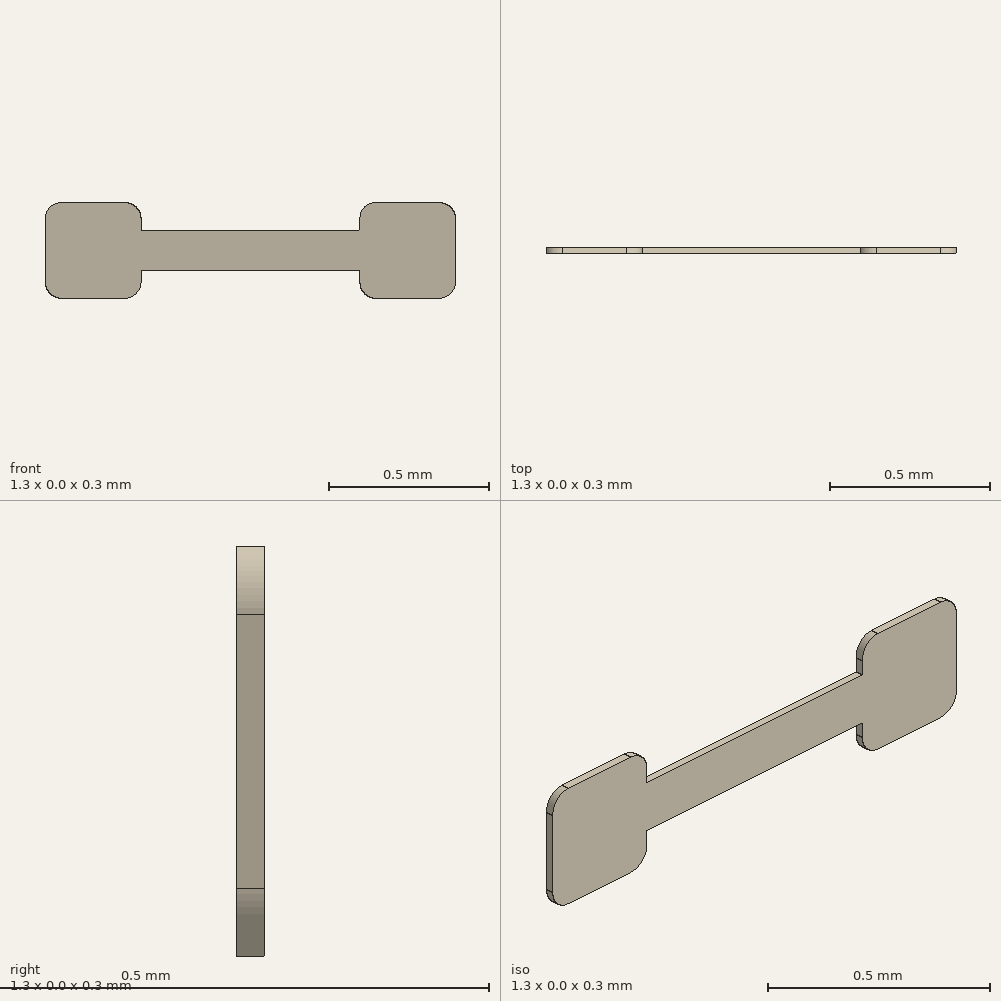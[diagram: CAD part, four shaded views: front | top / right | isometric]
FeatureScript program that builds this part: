
annotation { "Feature Type Name" : "Feature", "Feature Type Description" : "" }
export const myFeature = defineFeature(function(context is Context, id is Id, definition is map)
    precondition{}
    {
        {
            var Q0;
            Q0=qCreatedBy(makeId("Front.planeOp"),FACE);
            var sketch = newSketch(context, id + "F0", { "sketchPlane" : qUnion([Q0])});
            skLineSegment(sketch, "E0.bottom", {"start": v(0.05, 0) * mm, "end": v(0.25, 0) * mm});
            skLineSegment(sketch, "E0.top", {"start": v(0.05, 0.3) * mm, "end": v(0.25, 0.3) * mm});
            skLineSegment(sketch, "E0.left", {"start": v(0, 0.05) * mm, "end": v(0, 0.25) * mm});
            skLineSegment(sketch, "E0.right", {"start": v(0.3, 0.05) * mm, "end": v(0.3, 0.25) * mm});
            skLineSegment(sketch, "E1.bottom", {"start": v(0.3, 0.21) * mm, "end": v(0.99, 0.21) * mm});
            skLineSegment(sketch, "E1.top", {"start": v(0.3, 0.09) * mm, "end": v(0.99, 0.09) * mm});
            skLineSegment(sketch, "E1.left", {"start": v(0.3, 0.21) * mm, "end": v(0.3, 0.09) * mm});
            skLineSegment(sketch, "E1.right", {"start": v(0.99, 0.21) * mm, "end": v(0.99, 0.09) * mm});
            skLineSegment(sketch, "E2.bottom", {"start": v(1.04, 0.3) * mm, "end": v(1.24, 0.3) * mm});
            skLineSegment(sketch, "E2.top", {"start": v(1.04, 0) * mm, "end": v(1.24, 0) * mm});
            skLineSegment(sketch, "E2.left", {"start": v(0.99, 0.25) * mm, "end": v(0.99, 0.05) * mm});
            skLineSegment(sketch, "E2.right", {"start": v(1.29, 0.25) * mm, "end": v(1.29, 0.05) * mm});
            skLineSegment(sketch, "E3", {"start": v(0.3, 0.15) * mm, "end": v(0.99, 0.15) * mm, "construction": true});
            skPoint(sketch, "E4.visualSharp", {"position": v(0, 0.3) * mm});
            skArc(sketch, "E4.filletArc", {"start": v(0.05, 0.3) * mm, "mid": v(0.01, 0.29) * mm, "end": v(0, 0.25) * mm});
            skPoint(sketch, "E5.visualSharp", {"position": v(0.3, 0.3) * mm});
            skArc(sketch, "E5.filletArc", {"start": v(0.3, 0.25) * mm, "mid": v(0.29, 0.29) * mm, "end": v(0.25, 0.3) * mm});
            skPoint(sketch, "E6.visualSharp", {"position": v(0, 0) * mm});
            skArc(sketch, "E6.filletArc", {"start": v(0, 0.05) * mm, "mid": v(0.01, 0.01) * mm, "end": v(0.05, 0) * mm});
            skPoint(sketch, "E7.visualSharp", {"position": v(0.3, 0) * mm});
            skArc(sketch, "E7.filletArc", {"start": v(0.25, 0) * mm, "mid": v(0.29, 0.01) * mm, "end": v(0.3, 0.05) * mm});
            skPoint(sketch, "E8.visualSharp", {"position": v(0.99, 0.3) * mm});
            skArc(sketch, "E8.filletArc", {"start": v(1.04, 0.3) * mm, "mid": v(1, 0.29) * mm, "end": v(0.99, 0.25) * mm});
            skPoint(sketch, "E9.visualSharp", {"position": v(0.99, 0) * mm});
            skArc(sketch, "E9.filletArc", {"start": v(0.99, 0.05) * mm, "mid": v(1, 0.01) * mm, "end": v(1.04, 0) * mm});
            skPoint(sketch, "E10.visualSharp", {"position": v(1.29, 0) * mm});
            skArc(sketch, "E10.filletArc", {"start": v(1.24, 0) * mm, "mid": v(1.27, 0.01) * mm, "end": v(1.29, 0.05) * mm});
            skPoint(sketch, "E11.visualSharp", {"position": v(1.29, 0.3) * mm});
            skArc(sketch, "E11.filletArc", {"start": v(1.29, 0.25) * mm, "mid": v(1.27, 0.29) * mm, "end": v(1.24, 0.3) * mm});
            skSolve(sketch);
        }
        {
            var Q0;
            Q0 = qSketchRegion(id + "F0", true);
            extrude(context, id + "F1", {"entities" : qUnion([Q0]), "depth" : 0.02 * mm, "offsetDistance" : 25 * mm});
        }
    });
